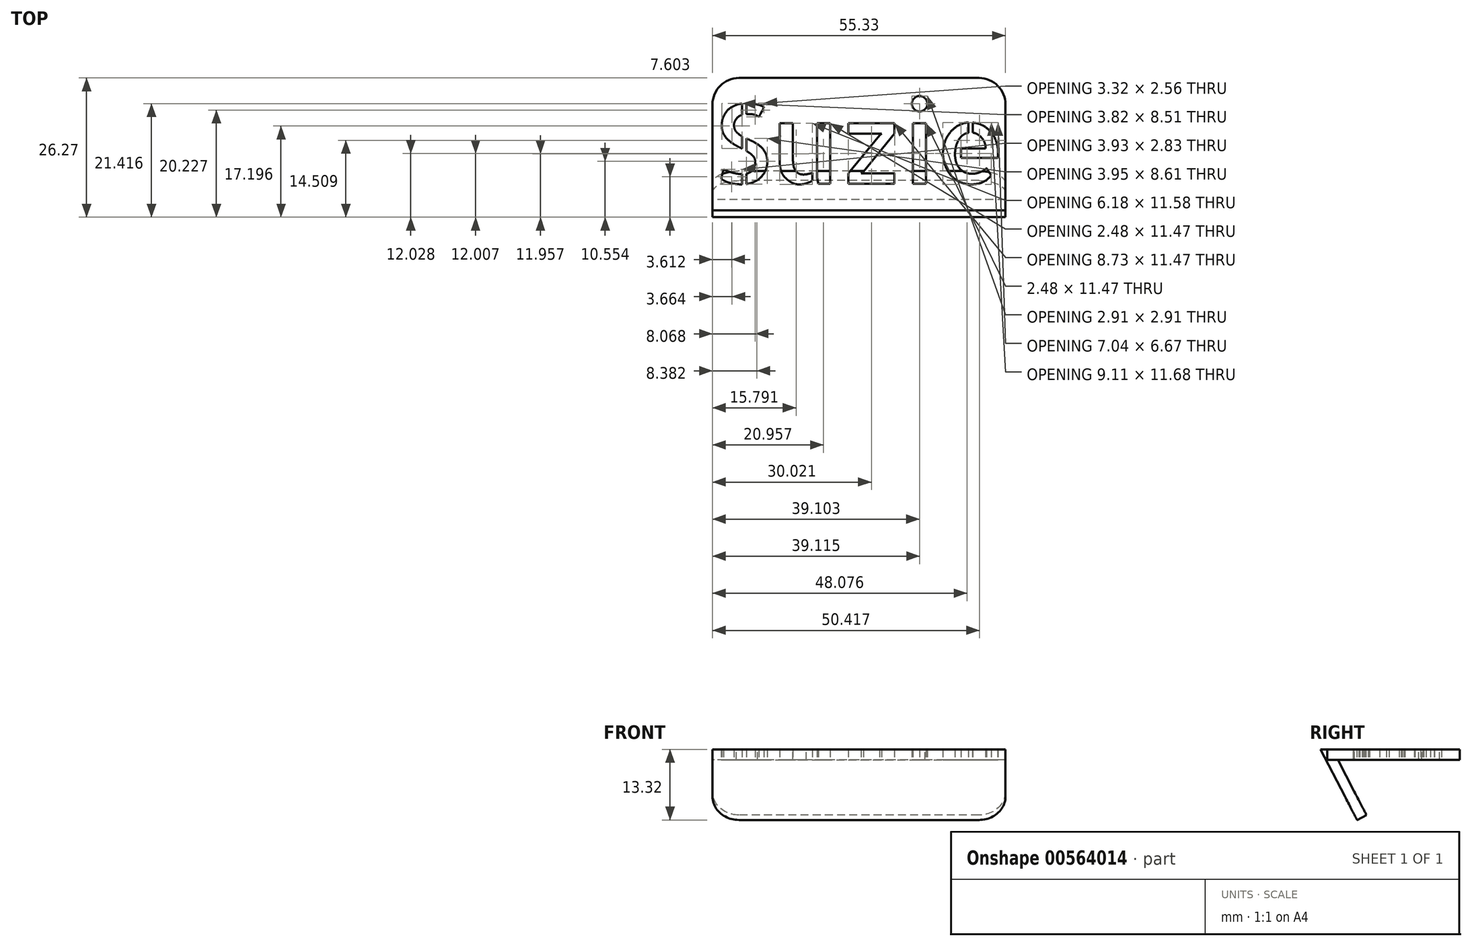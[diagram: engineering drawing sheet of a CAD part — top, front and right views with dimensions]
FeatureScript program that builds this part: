
annotation { "Feature Type Name" : "Feature", "Feature Type Description" : "" }
export const myFeature = defineFeature(function(context is Context, id is Id, definition is map)
    precondition{}
    {
        {
            var Q0;
            Q0=qCreatedBy(makeId("Top.planeOp"),FACE);
            var sketch = newSketch(context, id + "F0", { "sketchPlane" : qUnion([Q0])});
            skLineSegment(sketch, "E0.bottom", {"start": v(-23.58, 12.5) * mm, "end": v(31.75, 12.5) * mm});
            skLineSegment(sketch, "E0.top", {"start": v(-23.58, -12.5) * mm, "end": v(31.75, -12.5) * mm});
            skLineSegment(sketch, "E0.left", {"start": v(-23.58, 12.5) * mm, "end": v(-23.58, -12.5) * mm});
            skLineSegment(sketch, "E0.right", {"start": v(31.75, 12.5) * mm, "end": v(31.75, -12.5) * mm});
            skText(sketch, "E1", { "text": "Suzie", "fontName": "AllertaStencil-Regular.ttf"});
            const initialGuessF0  = {"E1": [-0.02358, -0.0075, 1, 0, 0.015]};
            skSetInitialGuess(sketch, initialGuessF0);
            skSolve(sketch);
        }
        {
            var Q0;
            Q0=makeQuery(id+"F0.imprint","IMPRINT",FACE,{"disambiguationData":[TD([[makeQuery(id+"F0.imprint","IMPRINT",EDGE,{"derivedFrom":sQuery(id+"F0.wireOp",EDGE,"E0.bottom")}),-1.0]])]});
            extrude(context, id + "F1", {"entities" : qUnion([Q0]), "depth" : 2 * mm, "offsetDistance" : 25 * mm});
        }
        {
            var Q0;
            {var subQ0=sQuery(id+"F0.wireOp",EDGE,"E0.left");Q0=makeQuery(id+"FYEOEdhl7jzHk82_2.opBoolean","MERGE",FACE,{"derivedFrom":[makeQuery(id+"F1.opExtrude","SWEPT_FACE",FACE,{"disambiguationData":[OSD([subQ0])]}),makeQuery(id+"FOv1BJgTRWeWuMw_1.opExtrude","CAP_FACE",FACE,{"disambiguationData":[OSD([sQuery(id+"F0.wireOp",EDGE,"E0.bottom"),subQ0,sQuery(id+"Fjco5yBOxZZxTCI_1.wireOp",EDGE,"TpTMtmOo-qoIM-rLEy-p7IH-mKgsBanMGF23"),sQuery(id+"Fjco5yBOxZZxTCI_1.wireOp",EDGE,"Ja6BvVoQ-cpFi-Lcom-cL8s-5xC4kZiynyNl"),sQuery(id+"Fjco5yBOxZZxTCI_1.wireOp",EDGE,"utNyaJ8P-FD6r-AD7x-tpFW-fHytfVhziHLl"),sQuery(id+"Fjco5yBOxZZxTCI_1.wireOp",EDGE,"xGzW29bi-H5H8-ObLh-gdKj-mSPkAtMAUUzO")])],"isStart":true})]});}
            var sketch = newSketch(context, id + "F2", { "sketchPlane" : qUnion([Q0])});
            skLineSegment(sketch, "E2", {"start": v(11.52, 2) * mm, "end": v(5.09, -10.4) * mm});
            skLineSegment(sketch, "E3", {"start": v(5.09, -10.4) * mm, "end": v(6.87, -11.32) * mm});
            skLineSegment(sketch, "E4", {"start": v(6.87, -11.32) * mm, "end": v(13.77, 2) * mm});
            skLineSegment(sketch, "E5", {"start": v(13.77, 2) * mm, "end": v(11.52, 2) * mm});
            skSolve(sketch);
        }
        {
            var Q0;
            {var subQ4=sQuery(id+"F2.wireOp",EDGE,"E3");Q0=makeQuery(id+"F2.imprint","IMPRINT",FACE,{"disambiguationData":[TD([[makeQuery(id+"F2.imprint","IMPRINT",EDGE,{"derivedFrom":subQ4}),1.0]])]});}
            var Q1;
            Q1=makeQuery(id+"F1.opExtrude","SWEPT_FACE",FACE,{"disambiguationData":[OSD([sQuery(id+"F0.wireOp",EDGE,"E0.right")])]});
            extrude(context, id + "F3", {"entities" : qUnion([Q0]), "endBound" : BoundingType.UP_TO_SURFACE, "oppositeDirection" : true, "depth" : 75 * mm, "endBoundEntityFace" : qUnion([Q1]), "offsetDistance" : 25 * mm});
        }
        {
            var Q0;
            Q0=makeQuery(id+"F1.opExtrude","SWEPT_EDGE",EDGE,{"disambiguationData":[OSD([sQuery(id+"F0.wireOp",EDGE,"E0.bottom"),sQuery(id+"F0.wireOp",EDGE,"E0.left")])]});
            var Q1;
            Q1=makeQuery(id+"F1.opExtrude","SWEPT_EDGE",EDGE,{"disambiguationData":[OSD([sQuery(id+"F0.wireOp",EDGE,"E0.bottom"),sQuery(id+"F0.wireOp",EDGE,"E0.right")])]});
            var Q2;
            Q2=makeQuery(id+"F3.opExtrude","CAP_EDGE",EDGE,{"disambiguationData":[OSD([sQuery(id+"F2.wireOp",EDGE,"E3")])],"isStart":false});
            var Q3;
            Q3=makeQuery(id+"F3.opExtrude","CAP_EDGE",EDGE,{"disambiguationData":[OSD([sQuery(id+"F2.wireOp",EDGE,"E3")])],"isStart":true});
            var Q4;
            Q4=makeQuery(id+"F3.opExtrude","TWEAK_EDGE",EDGE,{"derivedFrom":[makeQuery(id+"F1.opExtrude","SWEPT_FACE",FACE,{"disambiguationData":[OSD([sQuery(id+"F0.wireOp",EDGE,"E0.right")])]}),makeQuery(id+"F2.imprint","IMPRINT",EDGE,{"derivedFrom":sQuery(id+"F2.wireOp",EDGE,"E3")})]});
            fillet(context, id + "F4", {"entities" : qUnion([Q0, Q1, Q2, Q3, Q4]), "radius" : 5 * mm, "tangentPropagation" : true, "allowEdgeOverflow" : false});
        }
    });
